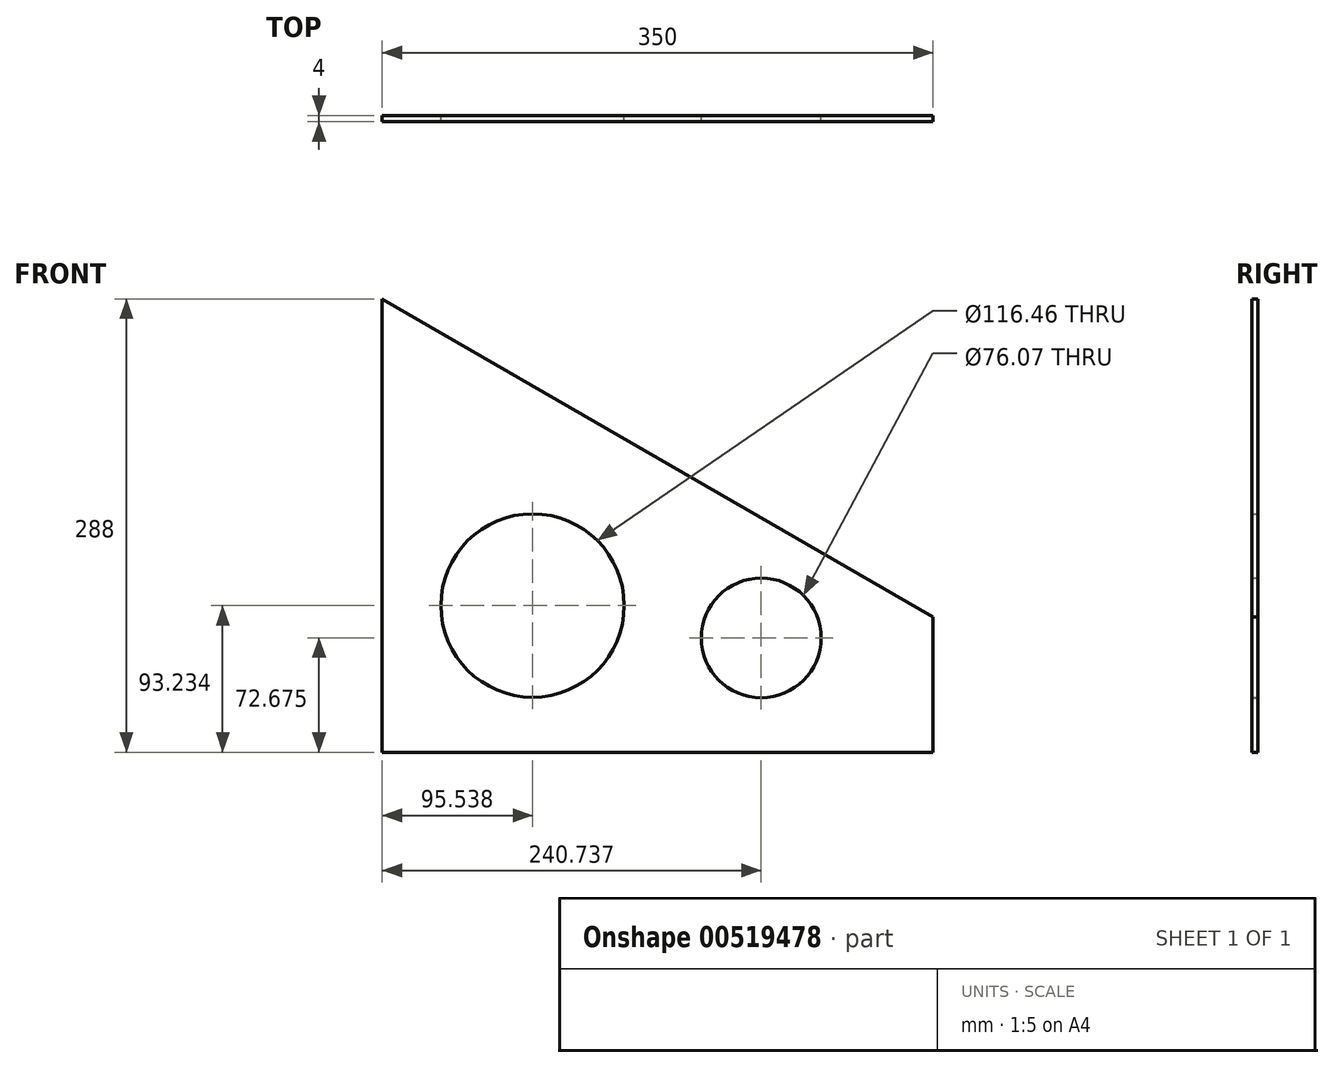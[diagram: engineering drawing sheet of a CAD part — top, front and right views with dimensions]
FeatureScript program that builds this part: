
annotation { "Feature Type Name" : "Feature", "Feature Type Description" : "" }
export const myFeature = defineFeature(function(context is Context, id is Id, definition is map)
    precondition{}
    {
        {
            var Q0;
            Q0=qCreatedBy(makeId("Front.planeOp"),FACE);
            var sketch = newSketch(context, id + "F0", { "sketchPlane" : qUnion([Q0])});
            skLineSegment(sketch, "E0", {"start": v(0, 0) * mm, "end": v(350, 0) * mm});
            skLineSegment(sketch, "E1", {"start": v(350, 86) * mm, "end": v(0, 288) * mm});
            skLineSegment(sketch, "E2", {"start": v(0, 288) * mm, "end": v(0, 0) * mm});
            skLineSegment(sketch, "E3", {"start": v(350, 0) * mm, "end": v(350, 86) * mm});
            skCircle(sketch, "E4", {"center": v(95.54, 93.23) * mm, "radius": 58.23 * mm});
            skCircle(sketch, "E5", {"center": v(240.74, 72.67) * mm, "radius": 38.03 * mm});
            skSolve(sketch);
        }
        {
            var Q0;
            Q0=makeQuery(id+"F0.imprint","IMPRINT",FACE,{"disambiguationData":[TD([[makeQuery(id+"F0.imprint","IMPRINT",EDGE,{"derivedFrom":sQuery(id+"F0.wireOp",EDGE,"E0")}),1.0]])]});
            extrude(context, id + "F1", {"entities" : qUnion([Q0]), "depth" : 4 * mm, "offsetDistance" : 25 * mm});
        }
    });
